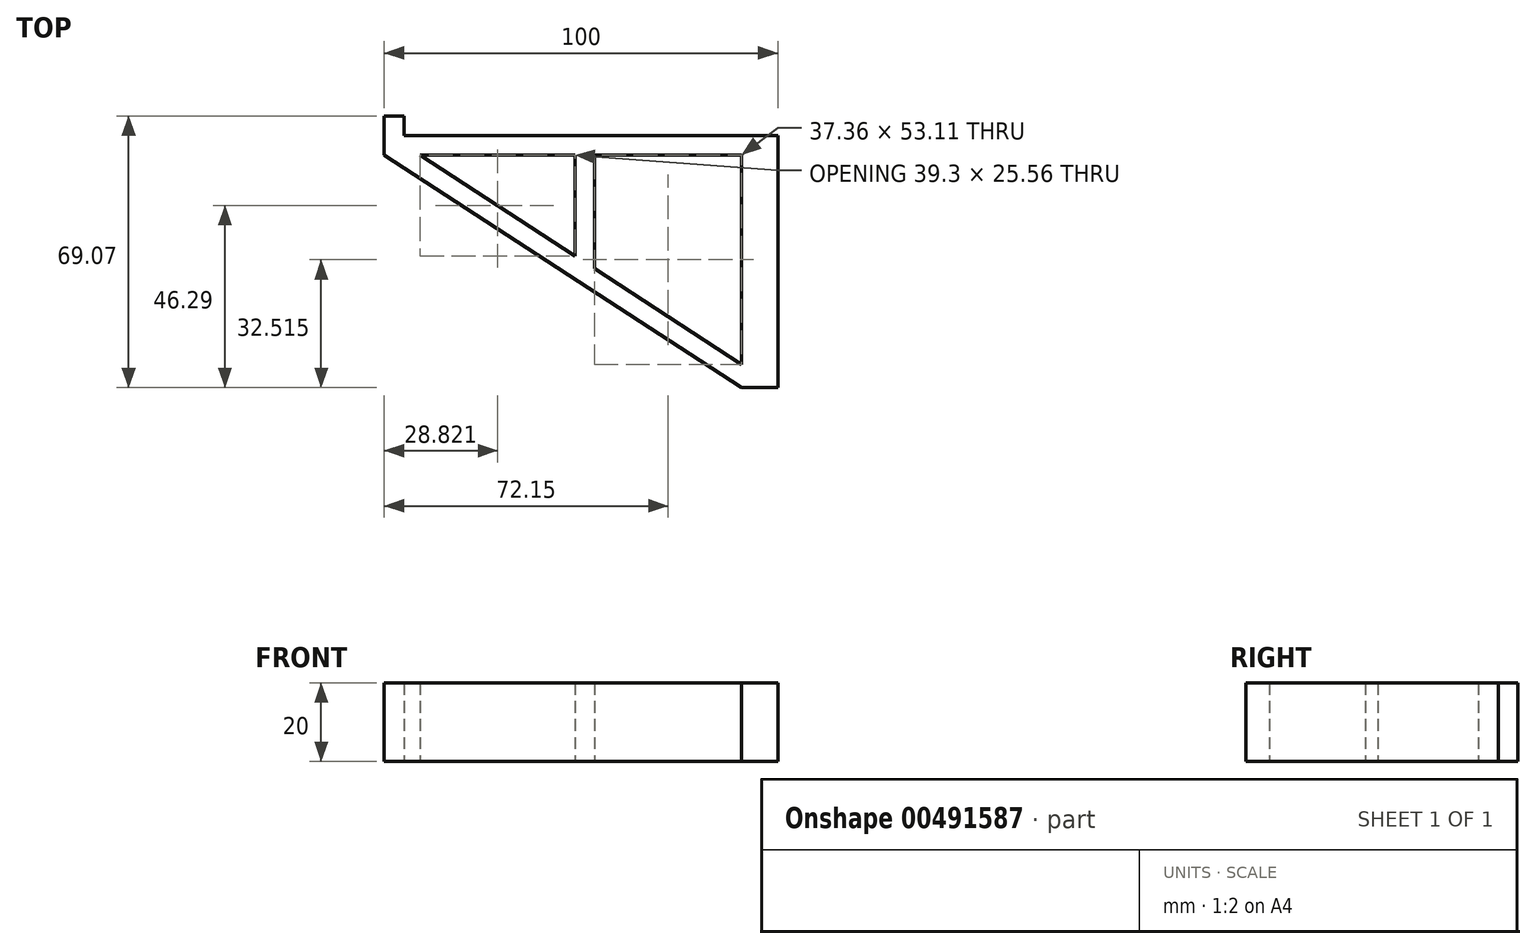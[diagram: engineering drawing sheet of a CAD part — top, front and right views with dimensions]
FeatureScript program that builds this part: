
annotation { "Feature Type Name" : "Feature", "Feature Type Description" : "" }
export const myFeature = defineFeature(function(context is Context, id is Id, definition is map)
    precondition{}
    {
        {
            var Q0;
            Q0=qCreatedBy(makeId("Top.planeOp"),FACE);
            var sketch = newSketch(context, id + "F0", { "sketchPlane" : qUnion([Q0])});
            skLineSegment(sketch, "E0", {"start": v(23.47, 0) * mm, "end": v(-71.53, 0) * mm});
            skLineSegment(sketch, "E1", {"start": v(-71.53, 0) * mm, "end": v(-71.53, 5) * mm});
            skLineSegment(sketch, "E2", {"start": v(-71.53, 5) * mm, "end": v(-76.53, 5) * mm});
            skLineSegment(sketch, "E3", {"start": v(-76.53, 5) * mm, "end": v(-76.53, 0) * mm});
            skLineSegment(sketch, "E4", {"start": v(-76.53, 0) * mm, "end": v(-76.53, -5) * mm});
            skLineSegment(sketch, "E5", {"start": v(-76.53, -5) * mm, "end": v(23.47, -5) * mm});
            skLineSegment(sketch, "E6", {"start": v(23.47, -5) * mm, "end": v(23.47, 0) * mm});
            skLineSegment(sketch, "E7", {"start": v(23.47, -5) * mm, "end": v(23.47, -64.07) * mm});
            skLineSegment(sketch, "E8", {"start": v(23.47, -64.07) * mm, "end": v(14.3, -64.07) * mm});
            skLineSegment(sketch, "E9", {"start": v(14.3, -64.07) * mm, "end": v(14.3, -5) * mm});
            skLineSegment(sketch, "E10", {"start": v(14.3, -64.07) * mm, "end": v(-76.53, -5) * mm});
            skLineSegment(sketch, "E11", {"start": v(23.47, -64.07) * mm, "end": v(-67.36, -5) * mm});
            skLineSegment(sketch, "E12", {"start": v(-28.06, -30.56) * mm, "end": v(-28.06, -5) * mm});
            skLineSegment(sketch, "E13", {"start": v(-23.06, -33.81) * mm, "end": v(-23.06, -5) * mm});
            skSolve(sketch);
        }
        {
            var Q0;
            Q0 = qSketchRegion(id + "F0", true);
            var Q1;
            {var subQ0=sQuery(id+"F0.wireOp",EDGE,"E12");Q1=makeQuery(id+"F0.imprint","IMPRINT",FACE,{"disambiguationData":[TD([[makeQuery(id+"F0.imprint","IMPRINT",EDGE,{"derivedFrom":subQ0}),-1.0]])]});}
            extrude(context, id + "F1", {"entities" : qUnion([Q0, Q1]), "depth" : 20 * mm});
        }
    });
